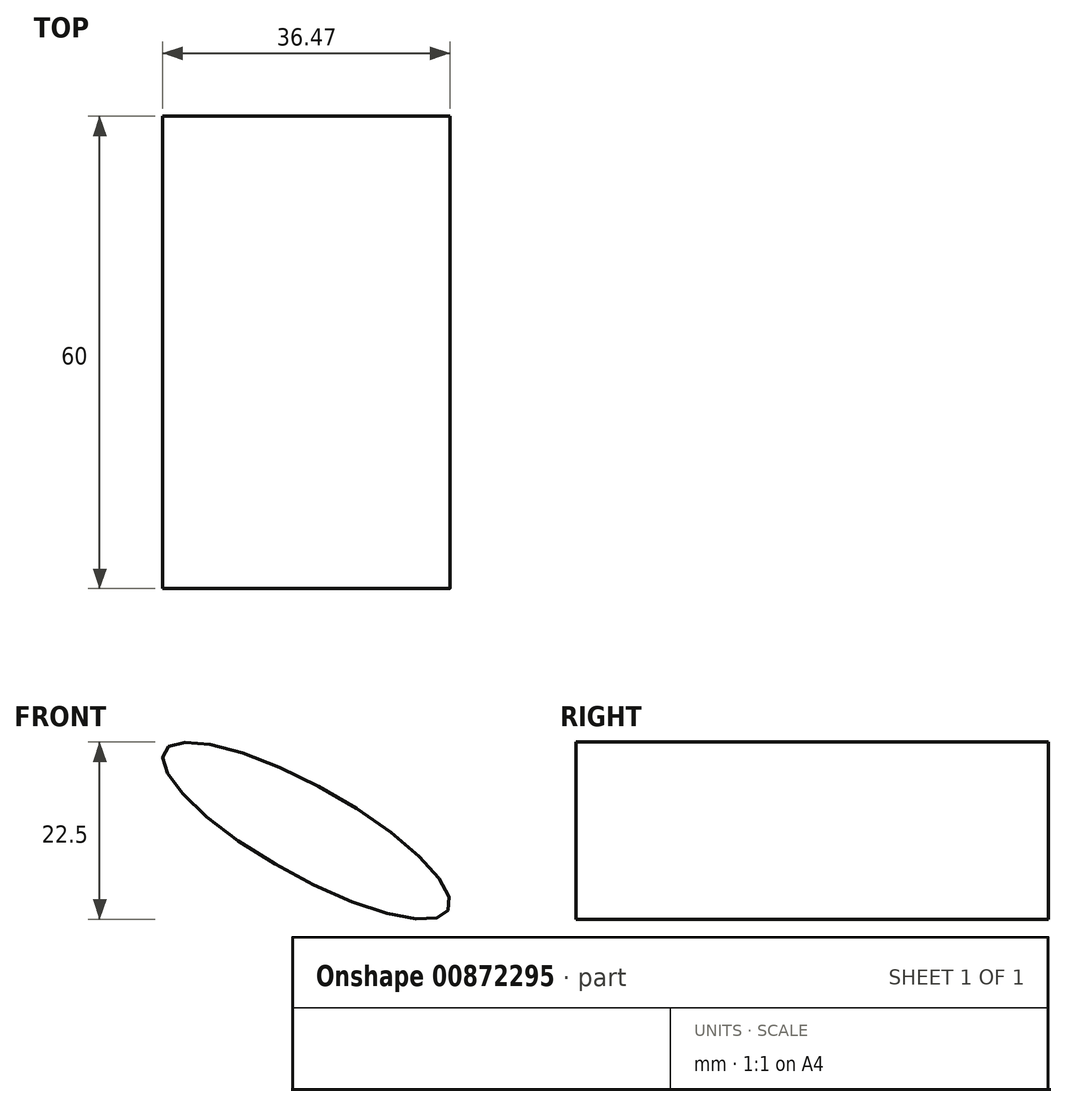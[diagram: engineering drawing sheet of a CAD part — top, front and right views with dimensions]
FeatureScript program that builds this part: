
annotation { "Feature Type Name" : "Feature", "Feature Type Description" : "" }
export const myFeature = defineFeature(function(context is Context, id is Id, definition is map)
    precondition{}
    {
        {
            var Q0;
            Q0=qCreatedBy(makeId("Front.planeOp"),FACE);
            var sketch = newSketch(context, id + "F0", { "sketchPlane" : qUnion([Q0])});
            skEllipse(sketch, "E0", {"center": v(-51.76, 53.34) * mm, "majorRadius": 20.66 * mm, "minorRadius": 5.68 * mm, "majorAxis": v(0.87, -0.49)});
            skSolve(sketch);
        }
        {
            var Q0;
            Q0=sQuery(id+"F0.wireOp",EDGE,"E0");
            extrude(context, id + "F1", {"bodyType" : ToolBodyType.SURFACE, "surfaceEntities" : qUnion([Q0]), "depth" : 60 * mm, "offsetDistance" : 25 * mm});
        }
    });
